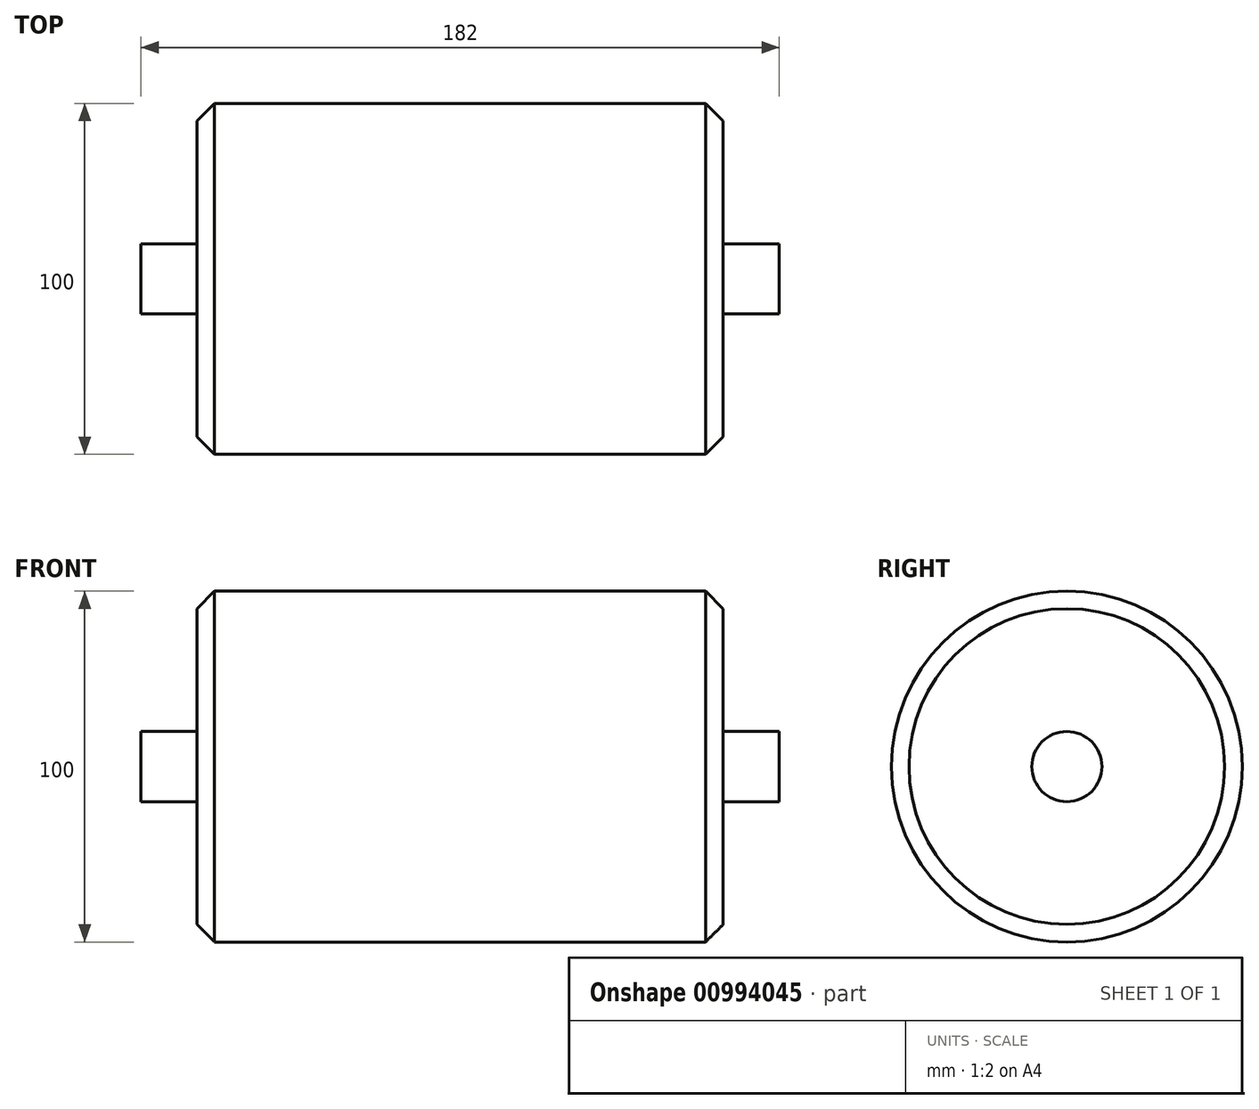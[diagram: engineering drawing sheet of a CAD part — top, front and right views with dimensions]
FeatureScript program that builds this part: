
annotation { "Feature Type Name" : "Feature", "Feature Type Description" : "" }
export const myFeature = defineFeature(function(context is Context, id is Id, definition is map)
    precondition{}
    {
        {
            var Q0;
            Q0=qCreatedBy(makeId("Right.planeOp"),FACE);
            var sketch = newSketch(context, id + "F0", { "sketchPlane" : qUnion([Q0])});
            skCircle(sketch, "E0", {"center": v(0, 0) * mm, "radius": 50 * mm});
            skCircle(sketch, "E1", {"center": v(0, 0) * mm, "radius": 10 * mm});
            skSolve(sketch);
        }
        {
            var Q0;
            Q0=makeQuery(id+"F0.imprint","IMPRINT",FACE,{"disambiguationData":[TD([[makeQuery(id+"F0.imprint","IMPRINT",EDGE,{"derivedFrom":sQuery(id+"F0.wireOp",EDGE,"E1")}),1.0]])]});
            extrude(context, id + "F1", {"entities" : qUnion([Q0]), "endBound" : BoundingType.SYMMETRIC, "depth" : 182 * mm, "offsetDistance" : 25 * mm});
        }
        {
            var Q0;
            Q0=makeQuery(id+"F0.imprint","IMPRINT",FACE,{"disambiguationData":[TD([[makeQuery(id+"F0.imprint","IMPRINT",EDGE,{"derivedFrom":sQuery(id+"F0.wireOp",EDGE,"E0")}),1.0]])]});
            extrude(context, id + "F2", {"entities" : qUnion([Q0]), "operationType" : NewBodyOperationType.ADD, "endBound" : BoundingType.SYMMETRIC, "depth" : 150 * mm, "offsetDistance" : 25 * mm});
        }
        {
            var Q0;
            Q0=makeQuery(id+"F2.opExtrude","CAP_EDGE",EDGE,{"disambiguationData":[OSD([sQuery(id+"F0.wireOp",EDGE,"E0")])],"isStart":false});
            var Q1;
            Q1=makeQuery(id+"F2.opExtrude","CAP_EDGE",EDGE,{"disambiguationData":[OSD([sQuery(id+"F0.wireOp",EDGE,"E0")])],"isStart":true});
            chamfer(context, id + "F3", {"entities" : qUnion([Q0, Q1]), "chamferType" : ChamferType.OFFSET_ANGLE, "width" : 5 * mm, "oppositeDirection" : false, "angle" : 45 * degree, "tangentPropagation" : true});
        }
    });
